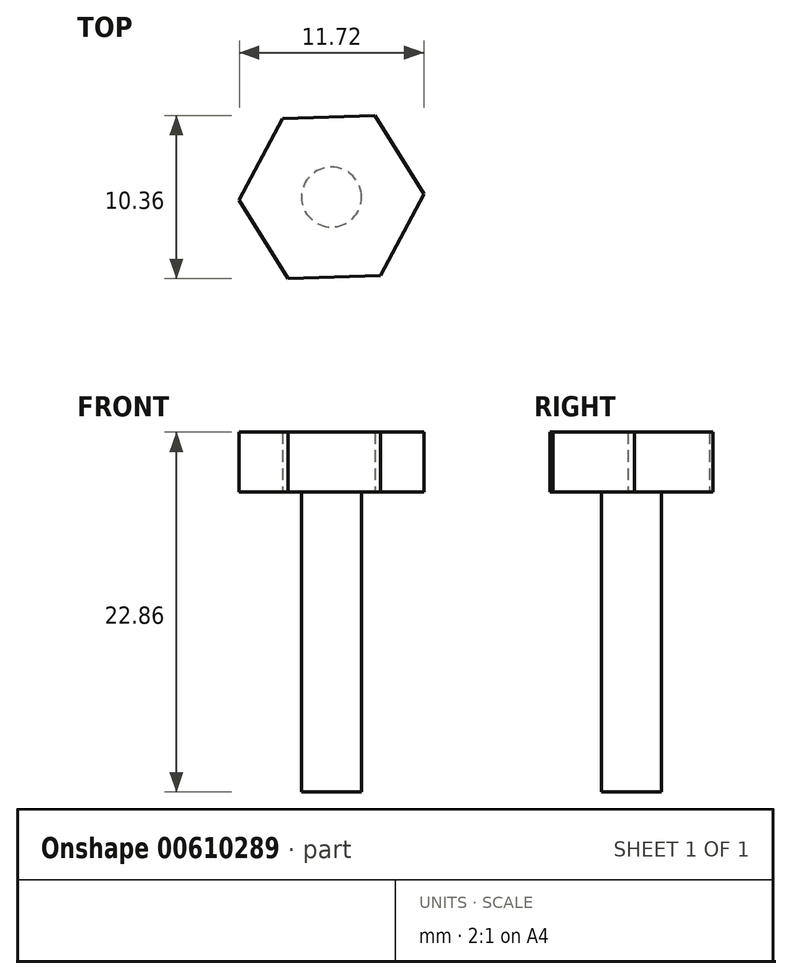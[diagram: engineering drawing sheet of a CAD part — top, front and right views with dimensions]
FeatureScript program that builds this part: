
annotation { "Feature Type Name" : "Feature", "Feature Type Description" : "" }
export const myFeature = defineFeature(function(context is Context, id is Id, definition is map)
    precondition{}
    {
        {
            var Q0;
            Q0=qCreatedBy(makeId("Top.planeOp"),FACE);
            var sketch = newSketch(context, id + "F0", { "sketchPlane" : qUnion([Q0])});
            skCircle(sketch, "E0", {"center": v(0, 0) * mm, "radius": 1.9 * mm});
            skSolve(sketch);
        }
        {
            var Q0;
            Q0=makeQuery(id+"F0.imprint","IMPRINT",FACE,{"disambiguationData":[TD([[makeQuery(id+"F0.imprint","IMPRINT",EDGE,{"derivedFrom":sQuery(id+"F0.wireOp",EDGE,"E0")}),1.0]])]});
            extrude(context, id + "F1", {"entities" : qUnion([Q0]), "depth" : 19.05 * mm, "offsetDistance" : 25.4 * mm});
        }
        {
            var Q0;
            Q0=makeQuery(id+"F1.opExtrude","CAP_FACE",FACE,{"disambiguationData":[OSD([sQuery(id+"F0.wireOp",EDGE,"E0")])],"isStart":false});
            var sketch = newSketch(context, id + "F2", { "sketchPlane" : qUnion([Q0])});
            skCircle(sketch, "E1.cCircle", {"center": v(0, 0) * mm, "radius": 5.08 * mm, "construction": true});
            skLineSegment(sketch, "E1.0", {"start": v(2.75, 5.18) * mm, "end": v(5.86, 0.2) * mm});
            skLineSegment(sketch, "E1.1", {"start": v(5.86, 0.2) * mm, "end": v(3.1, -4.97) * mm});
            skLineSegment(sketch, "E1.2", {"start": v(3.1, -4.97) * mm, "end": v(-2.75, -5.18) * mm});
            skLineSegment(sketch, "E1.3", {"start": v(-2.75, -5.18) * mm, "end": v(-5.86, -0.2) * mm});
            skLineSegment(sketch, "E1.4", {"start": v(-5.86, -0.2) * mm, "end": v(-3.1, 4.97) * mm});
            skLineSegment(sketch, "E1.5", {"start": v(-3.1, 4.97) * mm, "end": v(2.75, 5.18) * mm});
            skPoint(sketch, "E1.0.midPoint", {"position": v(4.3, 2.7) * mm});
            skSolve(sketch);
        }
        {
            var Q0;
            Q0 = qSketchRegion(id + "F2", true);
            extrude(context, id + "F3", {"entities" : qUnion([Q0]), "operationType" : NewBodyOperationType.ADD, "depth" : 3.8 * mm, "offsetDistance" : 25.4 * mm});
        }
    });
